# Revit family: PRD_AR_ShwrFttngsPckg_ShowerPanel_F5LT2020-F5LT2023
name_source: partatom
category: Plumbing Fixtures
units: mm (PartAtom-declared; Revit-internal decimal feet)

## family parameters
Cut with Voids When Loaded = No
Host = Face
OmniClass Number = 23.45.05.14.17
OmniClass Title = Showers
Part Type = Normal
Room Calculation Point = No
Round Connector Dimension = Use Diameter
Shared = No

## types (4) — shared parameters
AccentColour = chrome-look (glossy)
AdditionalConnections = no
AdjustableFlowTime = no
AssetType = Fixed
BasicColour = stainless steel-look
BodyMaterial = PRD_AR_StainlessSteel_SatinFinished
CasingMaterial = PRD_AR_StainlessSteel_SatinFinished_Dark
Category = Pr_40_20_87_75, Shower fittings package
Circulation = no
Color = stainless steel
CompatibleA3000Open = no
ConnectionWithPayWaterDispenser = not possible
Default Elevation = 1500 mm  [stored 4.92126 ft]
DiameterNominal = 15  [stored 0.0492126 ft]
DurationUnit = year
Finish = satin finished
FittingMaterial = PRD_AR_ChromatedBrass_HighPolished
FunctionalPrinciple = manual
HasTray = No
IfcExportAs = IfcSanitaryTerminalType
IfcExportType = SHOWER
InletSize = G 1/2 A
LockingMechanism = Top section, ceramic
Manufacturer = KWC Group AG
ManufacturerName = KWC Group AG
ManufacturerURL = www.kwc.com
Material = stainless steel
MaterialCasing = stainless steel
MaterialCodeCasing = 1.4301 Chrome Nickel steel V2A
MaterialFitting = brass-look
MinimumFlowPressure = 1 bar
NBSDescription = Shower fittings package
NBSReference = 45-35-70/330
NominalDepth = 90 mm  [stored 0.295276 ft]
NominalHeight = 1160 mm  [stored 3.80577 ft]
NominalLength = 1160 mm  [stored 3.80577 ft]
NominalWidth = 235 mm  [stored 0.770997 ft]
OverallDepth = 90 mm
OverallHeight = 1160 mm
OverallWidth = 235 mm
PositionOfWaterConnection = from top / backside
ProductInformation = http://pim.kwc.com
ProtectiveShutdown = no
ShowerMaterial = PRD_AR_StainlessSteel_SatinFinished
ShowerPipeDraining = no
ShowerType = Individual
Size = 235 x 1160 x 90 mm (W x H x D)
SoundInsulation = no
Status = New
SurfaceFinishCasing = satin finished
SurfaceFinishFitting = chromed
SurfaceTreatmentFitting = polished
TailorMade = no
TemperatureLimit = yes
ThermalDisinfection = yes
TypeOfMixing = with thermostat
TypeOfMounting = wall mounting
TypeOfOperation = manual operation
TypeOfShower = shower panel
URL = www.kwc.com
Uniclass2015Code = Pr_40_20_87_75
Uniclass2015Title = Shower fittings package
Uniclass2015Version = Products v1.32
Version = 1
VolumeFlowRate = 0.15 l/s at 3 bar
WarrantyDurationUnit = year
WaterConnection = hose (gland nut)
WithBackflowPreventer = yes
WithFilter = yes
WithRosettesOrCoverPlate = yes
WithSoapDish = no
zero-valued in all types: DrainSize

## per-type parameters (varying)
| type | BIMObjectName | DefaultAutomaticHygieneFlush | Description | Features | ForHandShower | HandShowerVisibility | HygieneFlushing | ModelNumber | Name | Parameterization | PositionOfPowerConnection | PowerSupplyConnection | ShowerHead | ShowerHeadVisibility | TypeOfPowerSupply | TypeOfSensor | WithShowerSet | WithTransformerOrPowerSupply |
| F5LT2020 | PRD_AR_ShowerFittingsPackage_ShowerPanel_F5LT2020 | fixed interval 24 hours | F5L-Therm stainless-steel shower panel for wall mounting with single-lever thermostat DN 15 and connecting nozzle for shower head. For connection to hot and cold water. Function block with integrated mixing cartridge and pre-assembled hygiene unit including sensor with control electronics to perform automatic water hygiene flushing, program-controlled thermal disinfection(additional bypass solenoid-operated flush valve cartridge necessary) and storage of statistical data. Thermostatically-controlled mixer cartridge with expansion element and active scald protection as well as adjustable and turn-proof temperature stop, and ceramic disc technology. All-metal construction, visible parts high-polished, chrome-plated. Connecting nozzles for separate required DN 15 KWC shower head with pre-fitted flow regulator 9.0l/min. Stainless steel housing with raised function surface and covercaps made of plastic. With adjustable and lockable connections with backflow preventer and strainers. Activated hygiene flushing, fixed interval of 24 hours. With option for parameterization and communication via optional, bidirectional remote control. Optional hygiene unit for battery operation with 6 V lithium battery (CR-P2) per fitting or separate power supply via plug-in power supply unit 6.75 V/12 V DC. | For connection to hot and cold water. Housing dimensions 235 x 1160 x 90 mm (W x H x D). Shower head and battery compartment including battery or power supply unit with extension cable must be ordered separately. | no | No | yes | 2030066509 | F5L-Therm stainless-steel shower panel F5LT2020 | remote control | from top / backside | 6.75 / 12 V DC | for separately shower head | Yes | Other | opto-electronic sensor | no | no |
| F5LT2021 | PRD_AR_ShowerFittingsPackage_ShowerPanel_F5LT2021 | fixed interval 24 hours | F5L-Therm stainless-steel shower panel for wall mounting with single-lever thermostat DN 15 and hand shower fitting kit. For connection to hot and cold water. Function block with integrated mixing cartridge and pre-assembled hygiene unit including sensor with control electronics to perform automatic water hygiene flushing, program-controlled thermal disinfection (additional bypass solenoid-operated flush valve cartridge necessary) and storage of statistical data. Thermostatically-controlled mixer cartridge with expansion element and active scald protection as well as adjustable and turn-proof temperature stop, and ceramic disc technology. All-metal construction, visible parts high-polished, chrome-plated. Pre-fitted chrome-plated brass shower rail with height-adjustable hand shower holder and chrome-plated brass hand shower, shower head with rain jet, diameter 110 mm, shower hose 900 mm. Housing made of stainless steel with raised function surface and cover caps made of plastic. With adjustable and lockable connections with backflow preventer and strainers. Activated hygiene flushing, fixed interval of 24 hours. With option for parameterization and communication via optional, bidirectional remote control. Optional hygiene unit for battery operation with 6 V lithium battery (CR-P2) per fitting or separate power supply via plug-in power supply unit 6.75 V/12 V DC. | For connection to hot and cold water. Housing dimensions 235 x 1160 x 90 mm (W x H x D). Battery compartment including battery or power supply unit with extension cable must be ordered separately. | yes | Yes | yes | 2030066510 | F5L-Therm stainless-steel shower panel with hand shower fitting kit F5LT2021 | remote control | from top / backside | 6.75 / 12 V DC |  | No | Other | opto-electronic sensor | yes | no |
| F5LT2022 | PRD_AR_ShowerFittingsPackage_ShowerPanel_F5LT2022 |  | F5L-Therm stainless-steel shower panel for wall mounting with single-lever thermostat DN 15 and connecting nozzle for shower head. For connection to hot and cold water. Function block with integrated mixing cartridge and mechanism for an optional water hygiene unit for automatic water hygiene flushing, program-controlled thermal disinfection (additional bypass solenoid-operated flush valve cartridge necessary) and storage of statistical data. Thermostatically-controlled mixer cartridge with expansion element and active scald protection as well as adjustable and turn-proof temperature stop, and ceramic disc technology. All-metal construction, visible parts high-polished, chrome-plated. Connecting nozzles for separate required DN 15 KWC shower head with pre-fitted flow regulator 9.0 l/min. Stainless steel housing with raised function surface and cover caps made of plastic. With adjustable and lockable connections with backflow preventer and strainers. | For connection to hot and cold water. Housing dimensions 235 x 1160 x 90 mm (W x H x D). Shower head must be ordered separately. | no | No | prepared | 2030066541 | F5L-Therm stainless-steel shower panel F5LT2022 |  |  |  | for separately shower head | Yes |  |  | no |  |
| F5LT2023 | PRD_AR_ShowerFittingsPackage_ShowerPanel_F5LT2023 |  | F5L-Therm stainless-steel shower panel for wall mounting with single-lever thermostat DN 15 and hand shower fitting kit. For connection to hot and cold water. Function block with integrated mixing cartridge and mechanism for an optional water hygiene unit for automatic water hygiene flushing, program-controlled thermal disinfection (additional bypass solenoid-operated flush valve cartridge necessary) and storage of statistical data. Thermostatically-controlled mixer cartridge with expansion element and active scald protection as well as adjustable and turn-proof temperature stop, and ceramic disc technology. All-metal construction, visible parts high-polished, chrome-plated. Pre-fitted chrome-plated brass shower rail with height-adjustable hand shower holder and chrome-plated brass hand shower, shower head with rain jet, diameter 110 mm, shower hose 900 mm. Housing made of stainless steel with raised function surface and cover caps made of plastic. With adjustable and lockable connections with backflow preventer and strainers. | For connection to hot and cold water. Housing dimensions 235 x 1160 x 90 mm (W x H x D). | yes | Yes | prepared | 2030066542 | F5L-Therm stainless-steel shower panel with hand shower fitting kit F5LT2023 |  |  |  |  | No |  |  | yes |  |

note: column(s) folded — value = type name in every type: Model, ModelReference

note: [stored X ft] marks values corroborated as IEEE doubles in the binary element streams (Revit-internal decimal feet)

## geometry (parser evidence)
native form markers: Sweep x6
no freeform markers — native parametric forms only
